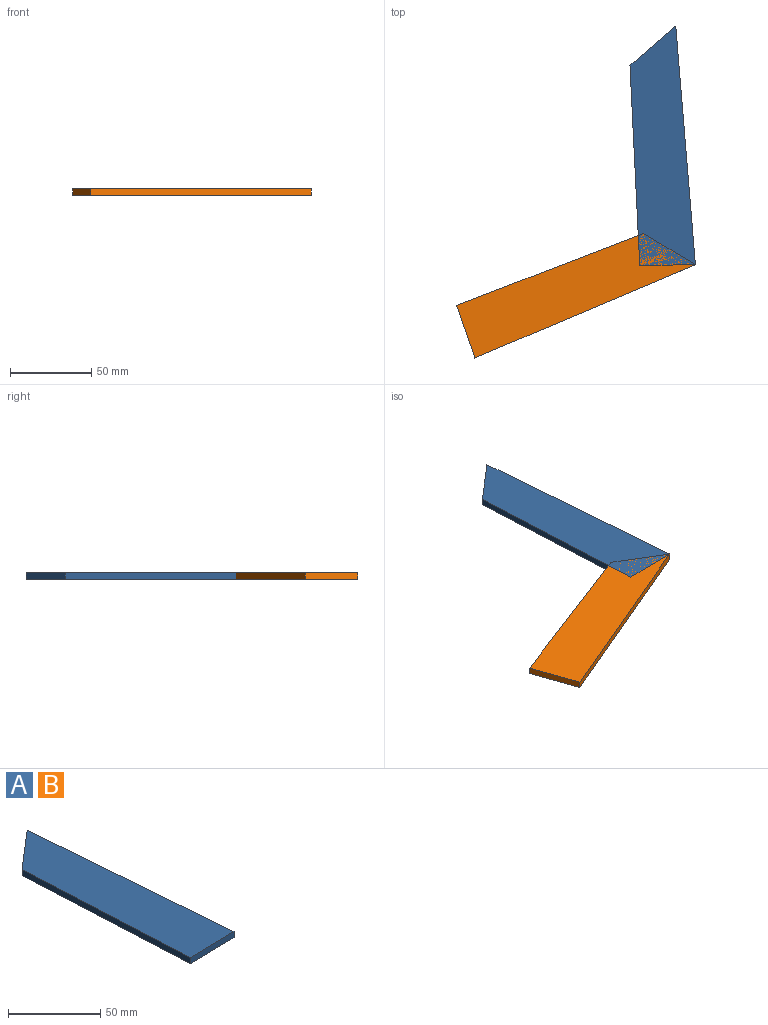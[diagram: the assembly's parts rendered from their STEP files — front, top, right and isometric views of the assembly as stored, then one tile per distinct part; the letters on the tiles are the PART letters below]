
ASSEMBLY  parts=2 mates=1
PART A: 6 faces, bbox 40.1x147x4 mm
  f0: plane 28.12x24.18mm, normal (-0.65,0.76,0), area 148.3mm2, adj f1,f3,f4,f5
  f1: plane 122.82x6.01mm, normal (-1,-0.05,0), area 491.9mm2, adj f0,f2,f4,f5
  f2: plane 34.14x4mm, normal (0.02,-1,0), area 136.6mm2, adj f1,f3,f4,f5
  f3: plane 146.45x12.03mm, normal (1,0.08,0), area 587.8mm2, adj f0,f2,f4,f5
  f4: plane 147x40.15mm, normal (0,0,1), area 4302.3mm2, adj f0,f1,f2,f3
  f5: plane 147x40.15mm, normal (0,0,-1), area 4302.3mm2, adj f0,f1,f2,f3
PART B: same geometry as A
PLACE A t=(103.63,-23.43,20.67)mm
PLACE B rot(axis=(0,0,-1),71.7deg) t=(103.34,-23.9,20.67)mm
MATE revolute B.f4 <-> A.f4  axis (0,0,1) through (210.43,-88.38,24.67)mm
